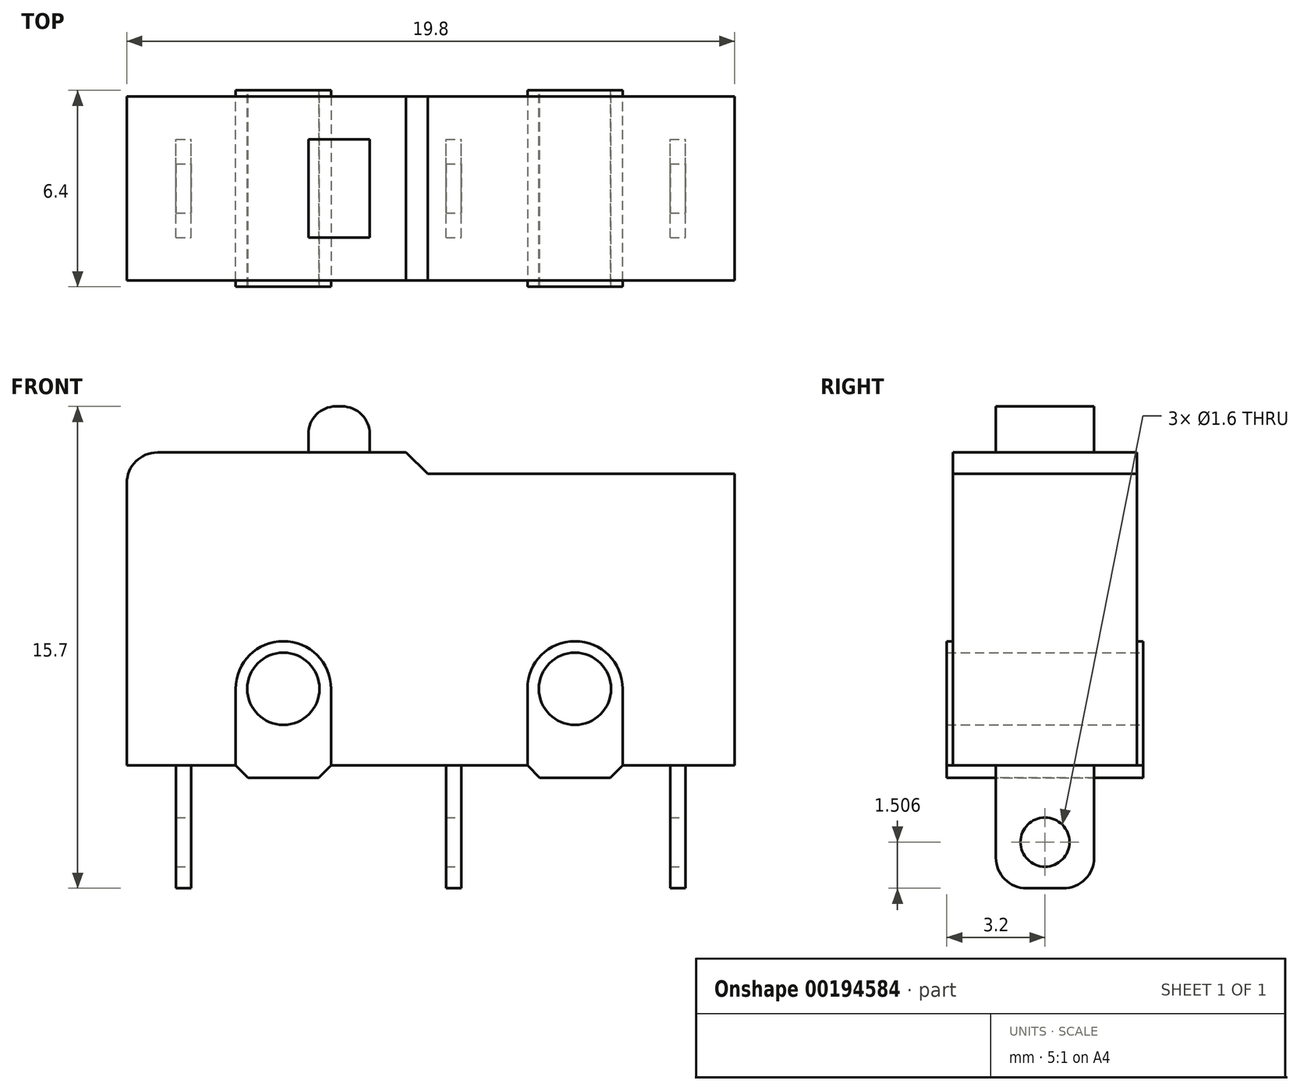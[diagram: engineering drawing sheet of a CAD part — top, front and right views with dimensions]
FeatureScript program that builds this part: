
annotation { "Feature Type Name" : "Feature", "Feature Type Description" : "" }
export const myFeature = defineFeature(function(context is Context, id is Id, definition is map)
    precondition{}
    {
        {
            var Q0;
            Q0=qCreatedBy(makeId("Front.planeOp"),FACE);
            var sketch = newSketch(context, id + "F0", { "sketchPlane" : qUnion([Q0])});
            skLineSegment(sketch, "E0.bottom", {"start": v(0, 0) * mm, "end": v(19.8, 0) * mm});
            skLineSegment(sketch, "E0.top", {"start": v(0, 10.2) * mm, "end": v(19.8, 10.2) * mm});
            skLineSegment(sketch, "E0.left", {"start": v(0, 0) * mm, "end": v(0, 10.2) * mm});
            skLineSegment(sketch, "E0.right", {"start": v(19.8, 0) * mm, "end": v(19.8, 10.2) * mm});
            skSolve(sketch);
        }
        {
            var Q0;
            Q0 = qSketchRegion(id + "F0", true);
            extrude(context, id + "F1", {"entities" : qUnion([Q0]), "depth" : 6 * mm});
        }
        {
            var Q0;
            Q0=makeQuery(id+"F1.opExtrude","CAP_FACE",FACE,{"disambiguationData":[OSD([sQuery(id+"F0.wireOp",EDGE,"E0.bottom"),sQuery(id+"F0.wireOp",EDGE,"E0.top"),sQuery(id+"F0.wireOp",EDGE,"E0.left"),sQuery(id+"F0.wireOp",EDGE,"E0.right")])],"isStart":false});
            var sketch = newSketch(context, id + "F2", { "sketchPlane" : qUnion([Q0])});
            skLineSegment(sketch, "E1", {"start": v(0, 2.5) * mm, "end": v(19.8, 2.5) * mm, "construction": true});
            skCircle(sketch, "E2", {"center": v(5.1, 2.5) * mm, "radius": 1.55 * mm});
            skCircle(sketch, "E3", {"center": v(14.6, 2.5) * mm, "radius": 1.55 * mm});
            skLineSegment(sketch, "E4", {"start": v(6.65, 2.5) * mm, "end": v(6.65, -0.4) * mm});
            skLineSegment(sketch, "E5", {"start": v(6.65, -0.4) * mm, "end": v(3.55, -0.4) * mm});
            skLineSegment(sketch, "E6", {"start": v(3.55, -0.4) * mm, "end": v(3.55, 2.5) * mm});
            skLineSegment(sketch, "E7", {"start": v(13.05, 2.5) * mm, "end": v(13.05, -0.4) * mm});
            skLineSegment(sketch, "E8", {"start": v(13.05, -0.4) * mm, "end": v(16.15, -0.4) * mm});
            skLineSegment(sketch, "E9", {"start": v(16.15, -0.4) * mm, "end": v(16.15, 2.5) * mm});
            skSolve(sketch);
        }
        {
            var Q0;
            Q0 = qSketchRegion(id + "F2", true);
            extrude(context, id + "F3", {"entities" : qUnion([Q0]), "operationType" : NewBodyOperationType.ADD, "depth" : 0.2 * mm});
        }
        {
            var Q0;
            Q0=makeQuery(id+"F3.opExtrude","CAP_FACE",FACE,{"disambiguationData":[OSD([sQuery(id+"F2.wireOp",EDGE,"E2"),sQuery(id+"F2.wireOp",EDGE,"E4"),sQuery(id+"F2.wireOp",EDGE,"E5"),sQuery(id+"F2.wireOp",EDGE,"E6")])],"isStart":false});
            var sketch = newSketch(context, id + "F4", { "sketchPlane" : qUnion([Q0])});
            skSolve(sketch);
        }
        {
            var Q0;
            Q0 = qSketchRegion(id + "F4", true);
            var Q1;
            Q1=makeQuery(id+"F4.imprint","IMPRINT",FACE,{"disambiguationData":[TD([[makeQuery(id+"F4.imprint","IMPRINT",EDGE,{"derivedFrom":makeQuery(id+"F3.opExtrude","CAP_EDGE",EDGE,{"disambiguationData":[OSD([sQuery(id+"F2.wireOp",EDGE,"E2")])],"isStart":false})}),1.0]])]});
            extrude(context, id + "F5", {"entities" : qUnion([Q0, Q1]), "operationType" : NewBodyOperationType.ADD, "oppositeDirection" : true, "depth" : 6.4 * mm});
        }
        {
            var Q0;
            Q0=makeQuery(id+"F3.opExtrude","CAP_FACE",FACE,{"disambiguationData":[OSD([sQuery(id+"F2.wireOp",EDGE,"E3"),sQuery(id+"F2.wireOp",EDGE,"E7"),sQuery(id+"F2.wireOp",EDGE,"E8"),sQuery(id+"F2.wireOp",EDGE,"E9")])],"isStart":false});
            extrude(context, id + "F6", {"entities" : qUnion([Q0]), "operationType" : NewBodyOperationType.ADD, "oppositeDirection" : true, "depth" : 6.4 * mm});
        }
        {
            var Q0;
            {var subQ0=sQuery(id+"F2.wireOp",EDGE,"E6");var subQ1=sQuery(id+"F2.wireOp",EDGE,"E5");Q0=makeQuery(id+"F5.boolean.opBoolean","MERGE",EDGE,{"derivedFrom":[makeQuery(id+"F3.opExtrude","SWEPT_EDGE",EDGE,{"disambiguationData":[OSD([subQ1,subQ0])]}),makeQuery(id+"F5.opExtrude","SWEPT_EDGE",EDGE,{"disambiguationData":[OSD([subQ1,subQ0])]})]});}
            var Q1;
            {var subQ0=sQuery(id+"F2.wireOp",EDGE,"E5");var subQ1=sQuery(id+"F2.wireOp",EDGE,"E4");Q1=makeQuery(id+"F5.boolean.opBoolean","MERGE",EDGE,{"derivedFrom":[makeQuery(id+"F3.opExtrude","SWEPT_EDGE",EDGE,{"disambiguationData":[OSD([subQ1,subQ0])]}),makeQuery(id+"F5.opExtrude","SWEPT_EDGE",EDGE,{"disambiguationData":[OSD([subQ1,subQ0])]})]});}
            var Q2;
            {var subQ0=sQuery(id+"F2.wireOp",EDGE,"E8");var subQ1=sQuery(id+"F2.wireOp",EDGE,"E7");Q2=makeQuery(id+"F6.boolean.opBoolean","MERGE",EDGE,{"derivedFrom":[makeQuery(id+"F3.opExtrude","SWEPT_EDGE",EDGE,{"disambiguationData":[OSD([subQ1,subQ0])]}),makeQuery(id+"F6.opExtrude","SWEPT_EDGE",EDGE,{"disambiguationData":[OSD([subQ1,subQ0])]})]});}
            var Q3;
            {var subQ0=sQuery(id+"F2.wireOp",EDGE,"E9");var subQ1=sQuery(id+"F2.wireOp",EDGE,"E8");Q3=makeQuery(id+"F6.boolean.opBoolean","MERGE",EDGE,{"derivedFrom":[makeQuery(id+"F3.opExtrude","SWEPT_EDGE",EDGE,{"disambiguationData":[OSD([subQ1,subQ0])]}),makeQuery(id+"F6.opExtrude","SWEPT_EDGE",EDGE,{"disambiguationData":[OSD([subQ1,subQ0])]})]});}
            chamfer(context, id + "F7", {"entities" : qUnion([Q0, Q1, Q2, Q3]), "width" : 0.4 * mm, "tangentPropagation" : true});
        }
        {
            var Q0;
            Q0=makeQuery(id+"F1.opExtrude","CAP_FACE",FACE,{"disambiguationData":[OSD([sQuery(id+"F0.wireOp",EDGE,"E0.bottom"),sQuery(id+"F0.wireOp",EDGE,"E0.top"),sQuery(id+"F0.wireOp",EDGE,"E0.left"),sQuery(id+"F0.wireOp",EDGE,"E0.right")])],"isStart":false});
            var sketch = newSketch(context, id + "F8", { "sketchPlane" : qUnion([Q0])});
            skLineSegment(sketch, "E10", {"start": v(9.1, 10.2) * mm, "end": v(9.8, 9.5) * mm});
            skLineSegment(sketch, "E11", {"start": v(9.8, 9.5) * mm, "end": v(19.8, 9.5) * mm});
            skLineSegment(sketch, "E12", {"start": v(19.8, 9.5) * mm, "end": v(19.8, 10.2) * mm});
            skLineSegment(sketch, "E13", {"start": v(19.8, 10.2) * mm, "end": v(9.1, 10.2) * mm});
            skSolve(sketch);
        }
        {
            var Q0;
            Q0 = qSketchRegion(id + "F8", true);
            extrude(context, id + "F9", {"entities" : qUnion([Q0]), "operationType" : NewBodyOperationType.REMOVE, "endBound" : BoundingType.THROUGH_ALL, "oppositeDirection" : true, "depth" : 25 * mm});
        }
        {
            var Q0;
            Q0=makeQuery(id+"F1.opExtrude","SWEPT_EDGE",EDGE,{"disambiguationData":[OSD([sQuery(id+"F0.wireOp",EDGE,"E0.top"),sQuery(id+"F0.wireOp",EDGE,"E0.left")])]});
            var Q1;
            Q1=makeQuery(id+"F9.boolean.opBoolean","COPY",EDGE,{"derivedFrom":makeQuery(id+"F9.opExtrude","SWEPT_EDGE",EDGE,{"disambiguationData":[OSD([sQuery(id+"F0.wireOp",EDGE,"E0.right"),sQuery(id+"F8.wireOp",EDGE,"E11"),sQuery(id+"F8.wireOp",EDGE,"E12")])]})});
            fillet(context, id + "F10", {"entities" : qUnion([Q0, Q1]), "radius" : 1 * mm, "tangentPropagation" : true, "allowEdgeOverflow" : false});
        }
        {
            var Q0;
            Q0=makeQuery(id+"F3.opExtrude","CAP_FACE",FACE,{"disambiguationData":[OSD([sQuery(id+"F2.wireOp",EDGE,"E2"),sQuery(id+"F2.wireOp",EDGE,"E4"),sQuery(id+"F2.wireOp",EDGE,"E5"),sQuery(id+"F2.wireOp",EDGE,"E6")])],"isStart":false});
            var sketch = newSketch(context, id + "F11", { "sketchPlane" : qUnion([Q0])});
            skLineSegment(sketch, "E14", {"start": v(0, 2.5) * mm, "end": v(17.98, 2.5) * mm, "construction": true});
            skPoint(sketch, "E15", {"position": v(5.1, 2.5) * mm});
            skSolve(sketch);
        }
        {
            var Q0;
            Q0=sQuery(id+"F11.wireOp",VERTEX,"E15");
            var Q1;
            Q1=makeQuery(id+"F1.opExtrude","SWEPT_BODY",BODY,{"disambiguationData":[OSD([sQuery(id+"F0.wireOp",EDGE,"E0.bottom"),sQuery(id+"F0.wireOp",EDGE,"E0.top"),sQuery(id+"F0.wireOp",EDGE,"E0.left"),sQuery(id+"F0.wireOp",EDGE,"E0.right")])]});
            hole(context, id + "F12", {"style" : HoleStyle.SIMPLE, "endStyle" : HoleEndStyle.THROUGH, "holeDiameter" : 2.35 * mm, "locations" : qUnion([Q0]), "scope" : qUnion([Q1]), "isTappedThrough" : true, "startStyle" : HoleStartStyle.PART});
        }
        {
            var Q0;
            Q0=makeQuery(id+"F3.opExtrude","CAP_FACE",FACE,{"disambiguationData":[OSD([sQuery(id+"F2.wireOp",EDGE,"E3"),sQuery(id+"F2.wireOp",EDGE,"E7"),sQuery(id+"F2.wireOp",EDGE,"E8"),sQuery(id+"F2.wireOp",EDGE,"E9")])],"isStart":false});
            var sketch = newSketch(context, id + "F13", { "sketchPlane" : qUnion([Q0])});
            skLineSegment(sketch, "E16", {"start": v(16.15, 2.5) * mm, "end": v(10.83, 2.5) * mm, "construction": true});
            skPoint(sketch, "E17", {"position": v(14.6, 2.5) * mm});
            skSolve(sketch);
        }
        {
            var Q0;
            Q0=sQuery(id+"F13.wireOp",VERTEX,"E17");
            var Q1;
            Q1=makeQuery(id+"F1.opExtrude","SWEPT_BODY",BODY,{"disambiguationData":[OSD([sQuery(id+"F0.wireOp",EDGE,"E0.bottom"),sQuery(id+"F0.wireOp",EDGE,"E0.top"),sQuery(id+"F0.wireOp",EDGE,"E0.left"),sQuery(id+"F0.wireOp",EDGE,"E0.right")])]});
            hole(context, id + "F14", {"style" : HoleStyle.SIMPLE, "endStyle" : HoleEndStyle.THROUGH, "holeDiameter" : 2.35 * mm, "locations" : qUnion([Q0]), "scope" : qUnion([Q1]), "isTappedThrough" : true, "startStyle" : HoleStartStyle.PART});
        }
        {
            var Q0;
            Q0=makeQuery(id+"F1.opExtrude","SWEPT_FACE",FACE,{"disambiguationData":[OSD([sQuery(id+"F0.wireOp",EDGE,"E0.top")])]});
            var sketch = newSketch(context, id + "F15", { "sketchPlane" : qUnion([Q0])});
            skLineSegment(sketch, "E18.bottom", {"start": v(5.91, -1.4) * mm, "end": v(7.91, -1.4) * mm});
            skLineSegment(sketch, "E18.top", {"start": v(5.91, -4.6) * mm, "end": v(7.91, -4.6) * mm});
            skLineSegment(sketch, "E18.left", {"start": v(5.91, -1.4) * mm, "end": v(5.91, -4.6) * mm});
            skLineSegment(sketch, "E18.right", {"start": v(7.91, -1.4) * mm, "end": v(7.91, -4.6) * mm});
            skLineSegment(sketch, "E19", {"start": v(5.91, -1.4) * mm, "end": v(5.91, 0) * mm, "construction": true});
            skLineSegment(sketch, "E20", {"start": v(5.91, -4.6) * mm, "end": v(5.91, -6) * mm, "construction": true});
            skSolve(sketch);
        }
        {
            var Q0;
            Q0 = qSketchRegion(id + "F15", true);
            extrude(context, id + "F16", {"entities" : qUnion([Q0]), "operationType" : NewBodyOperationType.ADD, "depth" : 1.5 * mm});
        }
        {
            var Q0;
            Q0=makeQuery(id+"F16.opExtrude","CAP_EDGE",EDGE,{"disambiguationData":[OSD([sQuery(id+"F15.wireOp",EDGE,"E18.left")])],"isStart":false});
            var Q1;
            Q1=makeQuery(id+"F16.opExtrude","CAP_EDGE",EDGE,{"disambiguationData":[OSD([sQuery(id+"F15.wireOp",EDGE,"E18.right")])],"isStart":false});
            fillet(context, id + "F17", {"entities" : qUnion([Q0, Q1]), "radius" : 0.9 * mm, "tangentPropagation" : true, "allowEdgeOverflow" : false});
        }
        {
            var Q0;
            {var subQ0=sQuery(id+"F0.wireOp",EDGE,"E0.left");var subQ4=sQuery(id+"F0.wireOp",EDGE,"E0.bottom");Q0=makeQuery(id+"F5.boolean.opBoolean","SPLIT",FACE,{"disambiguationData":[TD([makeQuery(id+"F1.opExtrude","SWEPT_FACE",FACE,{"disambiguationData":[OSD([subQ0])]})])],"derivedFrom":makeQuery(id+"F1.opExtrude","SWEPT_FACE",FACE,{"disambiguationData":[OSD([subQ4])]})});}
            var sketch = newSketch(context, id + "F18", { "sketchPlane" : qUnion([Q0])});
            skLineSegment(sketch, "E21.bottom", {"start": v(1.6, 4.6) * mm, "end": v(2.1, 4.6) * mm});
            skLineSegment(sketch, "E21.top", {"start": v(1.6, 1.4) * mm, "end": v(2.1, 1.4) * mm});
            skLineSegment(sketch, "E21.left", {"start": v(1.6, 4.6) * mm, "end": v(1.6, 1.4) * mm});
            skLineSegment(sketch, "E21.right", {"start": v(2.1, 4.6) * mm, "end": v(2.1, 1.4) * mm});
            skLineSegment(sketch, "E22.bottom", {"start": v(10.4, 4.6) * mm, "end": v(10.9, 4.6) * mm});
            skLineSegment(sketch, "E22.top", {"start": v(10.4, 1.4) * mm, "end": v(10.9, 1.4) * mm});
            skLineSegment(sketch, "E22.left", {"start": v(10.4, 4.6) * mm, "end": v(10.4, 1.4) * mm});
            skLineSegment(sketch, "E22.right", {"start": v(10.9, 4.6) * mm, "end": v(10.9, 1.4) * mm});
            skLineSegment(sketch, "E23.bottom", {"start": v(17.7, 4.6) * mm, "end": v(18.2, 4.6) * mm});
            skLineSegment(sketch, "E23.top", {"start": v(17.7, 1.4) * mm, "end": v(18.2, 1.4) * mm});
            skLineSegment(sketch, "E23.left", {"start": v(17.7, 4.6) * mm, "end": v(17.7, 1.4) * mm});
            skLineSegment(sketch, "E23.right", {"start": v(18.2, 4.6) * mm, "end": v(18.2, 1.4) * mm});
            skPoint(sketch, "E24.end.orphan", {"position": v(1.6, 0) * mm});
            skPoint(sketch, "E25.end.orphan", {"position": v(10.4, 0) * mm});
            skPoint(sketch, "E26.end.orphan", {"position": v(17.7, 0) * mm});
            skSolve(sketch);
        }
        {
            var Q0;
            Q0 = qSketchRegion(id + "F18", true);
            extrude(context, id + "F19", {"entities" : qUnion([Q0]), "operationType" : NewBodyOperationType.ADD, "depth" : 4 * mm});
        }
        {
            var Q0;
            Q0=makeQuery(id+"F19.opExtrude","SWEPT_FACE",FACE,{"disambiguationData":[OSD([sQuery(id+"F18.wireOp",EDGE,"E21.left")])]});
            var sketch = newSketch(context, id + "F20", { "sketchPlane" : qUnion([Q0])});
            skPoint(sketch, "E27", {"position": v(3, -2.5) * mm});
            skPoint(sketch, "E27.positionSnap0", {"position": v(3, -4) * mm});
            skSolve(sketch);
        }
        {
            var Q0;
            Q0=sQuery(id+"F20.wireOp",VERTEX,"E27");
            var Q1;
            Q1=makeQuery(id+"F1.opExtrude","SWEPT_BODY",BODY,{"disambiguationData":[OSD([sQuery(id+"F0.wireOp",EDGE,"E0.bottom"),sQuery(id+"F0.wireOp",EDGE,"E0.top"),sQuery(id+"F0.wireOp",EDGE,"E0.left"),sQuery(id+"F0.wireOp",EDGE,"E0.right")])]});
            hole(context, id + "F21", {"style" : HoleStyle.SIMPLE, "endStyle" : HoleEndStyle.THROUGH, "holeDiameter" : 1.6 * mm, "locations" : qUnion([Q0]), "scope" : qUnion([Q1]), "isTappedThrough" : true, "startStyle" : HoleStartStyle.PART});
        }
        {
            var Q0;
            Q0=makeQuery(id+"F19.opExtrude","CAP_EDGE",EDGE,{"disambiguationData":[OSD([sQuery(id+"F18.wireOp",EDGE,"E23.bottom")])],"isStart":false});
            var Q1;
            Q1=makeQuery(id+"F19.opExtrude","CAP_EDGE",EDGE,{"disambiguationData":[OSD([sQuery(id+"F18.wireOp",EDGE,"E22.bottom")])],"isStart":false});
            var Q2;
            Q2=makeQuery(id+"F19.opExtrude","CAP_EDGE",EDGE,{"disambiguationData":[OSD([sQuery(id+"F18.wireOp",EDGE,"E21.bottom")])],"isStart":false});
            var Q3;
            Q3=makeQuery(id+"F19.opExtrude","CAP_EDGE",EDGE,{"disambiguationData":[OSD([sQuery(id+"F18.wireOp",EDGE,"E21.top")])],"isStart":false});
            var Q4;
            Q4=makeQuery(id+"F19.opExtrude","CAP_EDGE",EDGE,{"disambiguationData":[OSD([sQuery(id+"F18.wireOp",EDGE,"E22.top")])],"isStart":false});
            var Q5;
            Q5=makeQuery(id+"F19.opExtrude","CAP_EDGE",EDGE,{"disambiguationData":[OSD([sQuery(id+"F18.wireOp",EDGE,"E23.top")])],"isStart":false});
            fillet(context, id + "F22", {"entities" : qUnion([Q0, Q1, Q2, Q3, Q4, Q5]), "radius" : 1 * mm, "tangentPropagation" : true, "allowEdgeOverflow" : false});
        }
    });
